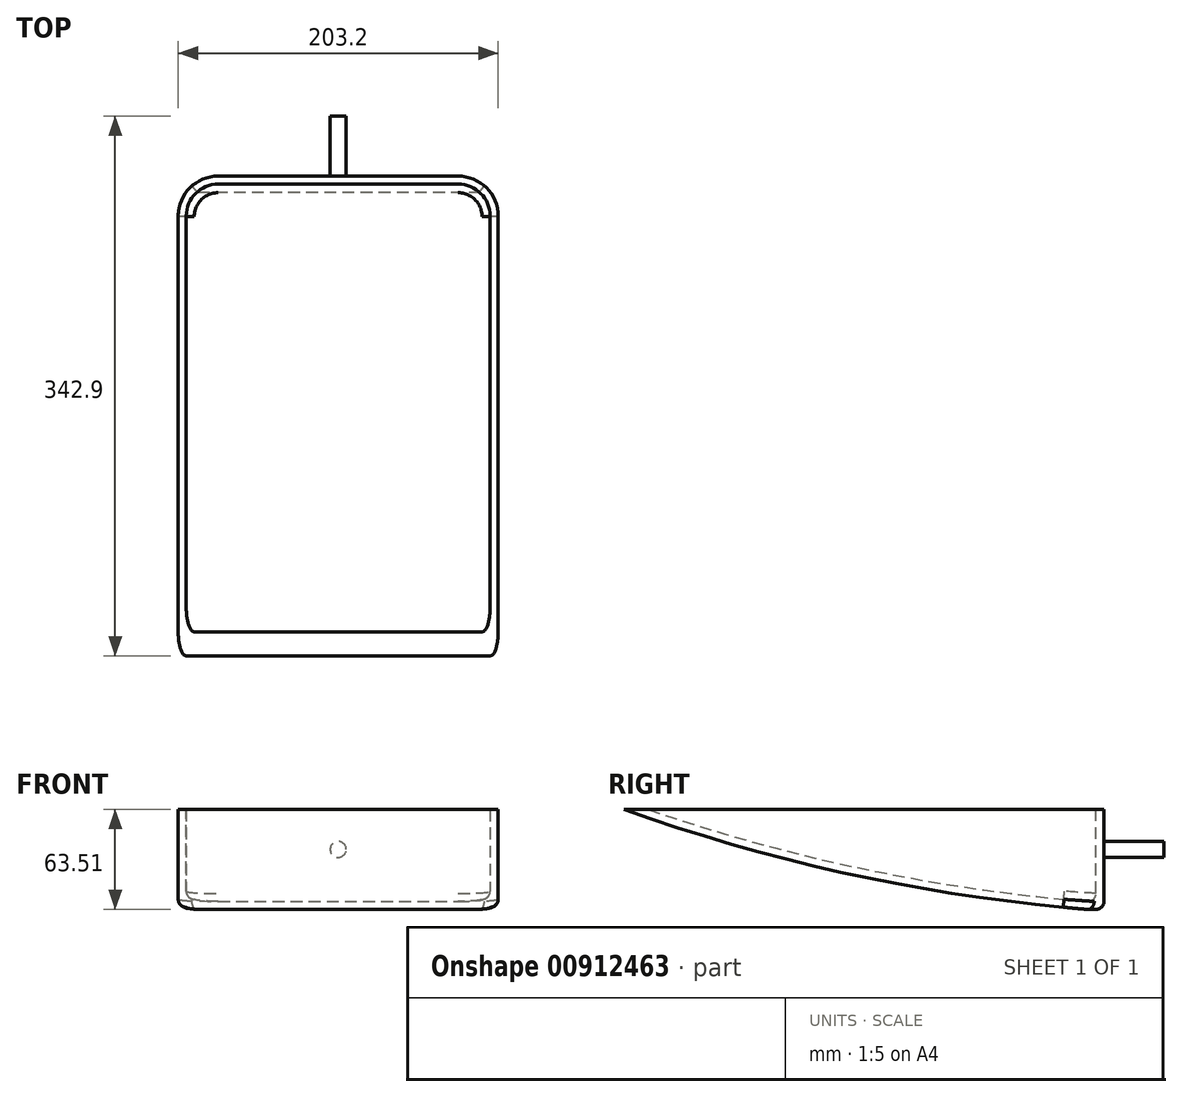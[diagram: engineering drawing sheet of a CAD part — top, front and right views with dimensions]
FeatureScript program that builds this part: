
annotation { "Feature Type Name" : "Feature", "Feature Type Description" : "" }
export const myFeature = defineFeature(function(context is Context, id is Id, definition is map)
    precondition{}
    {
        {
            var Q0;
            Q0=qCreatedBy(makeId("Top.planeOp"),FACE);
            var sketch = newSketch(context, id + "F0", { "sketchPlane" : qUnion([Q0])});
            skLineSegment(sketch, "E0.bottom", {"start": v(-50.23, 269.87) * mm, "end": v(152.97, 269.87) * mm});
            skLineSegment(sketch, "E0.top", {"start": v(-50.23, -34.93) * mm, "end": v(152.97, -34.93) * mm});
            skLineSegment(sketch, "E0.left", {"start": v(-50.23, 269.87) * mm, "end": v(-50.23, -34.93) * mm});
            skLineSegment(sketch, "E0.right", {"start": v(152.97, 269.87) * mm, "end": v(152.97, -34.93) * mm});
            skSolve(sketch);
        }
        {
            var Q0;
            Q0=makeQuery(id+"F0.imprint","IMPRINT",FACE,{"disambiguationData":[TD([[makeQuery(id+"F0.imprint","IMPRINT",EDGE,{"derivedFrom":sQuery(id+"F0.wireOp",EDGE,"E0.bottom")}),-1.0]])]});
            extrude(context, id + "F1", {"entities" : qUnion([Q0]), "depth" : 63.5 * mm, "offsetDistance" : 25.4 * mm});
        }
        {
            var Q0;
            Q0=makeQuery(id+"F1.opExtrude","SWEPT_FACE",FACE,{"disambiguationData":[OSD([sQuery(id+"F0.wireOp",EDGE,"E0.bottom")])]});
            var sketch = newSketch(context, id + "F2", { "sketchPlane" : qUnion([Q0])});
            skCircle(sketch, "E1", {"center": v(-51.37, 38.1) * mm, "radius": 5.08 * mm});
            skSolve(sketch);
        }
        {
            var Q0;
            Q0=makeQuery(id+"F2.imprint","IMPRINT",FACE,{"disambiguationData":[TD([[makeQuery(id+"F2.imprint","IMPRINT",EDGE,{"derivedFrom":sQuery(id+"F2.wireOp",EDGE,"E1")}),1.0]])]});
            extrude(context, id + "F3", {"entities" : qUnion([Q0]), "operationType" : NewBodyOperationType.ADD, "depth" : 38.1 * mm, "offsetDistance" : 25.4 * mm});
        }
        {
            var Q0;
            Q0=makeQuery(id+"F1.opExtrude","SWEPT_EDGE",EDGE,{"disambiguationData":[OSD([sQuery(id+"F0.wireOp",EDGE,"E0.bottom"),sQuery(id+"F0.wireOp",EDGE,"E0.left")])]});
            var Q1;
            Q1=makeQuery(id+"F1.opExtrude","SWEPT_EDGE",EDGE,{"disambiguationData":[OSD([sQuery(id+"F0.wireOp",EDGE,"E0.bottom"),sQuery(id+"F0.wireOp",EDGE,"E0.right")])]});
            fillet(context, id + "F4", {"entities" : qUnion([Q0, Q1]), "radius" : 25.4 * mm, "tangentPropagation" : true, "allowEdgeOverflow" : false});
        }
        {
            var Q0;
            Q0=makeQuery(id+"F1.opExtrude","SWEPT_FACE",FACE,{"disambiguationData":[OSD([sQuery(id+"F0.wireOp",EDGE,"E0.right")])]});
            var sketch = newSketch(context, id + "F5", { "sketchPlane" : qUnion([Q0])});
            skArc(sketch, "E2", {"start": v(-34.93, 63.5) * mm, "mid": v(110.25, 21.99) * mm, "end": v(259.63, 0) * mm});
            skLineSegment(sketch, "E3", {"start": v(-34.93, 63.5) * mm, "end": v(-61, -69.5) * mm});
            skLineSegment(sketch, "E4", {"start": v(-61, -69.5) * mm, "end": v(259.63, 0) * mm});
            skSolve(sketch);
        }
        {
            var Q0;
            {var subQ1=sQuery(id+"F0.wireOp",EDGE,"E0.right");var subQ6=makeQuery(id+"F1.opExtrude","CAP_EDGE",EDGE,{"disambiguationData":[OSD([subQ1])],"isStart":true});Q0=makeQuery(id+"F5.imprint","IMPRINT",FACE,{"disambiguationData":[TD([[makeQuery(id+"F5.imprint","IMPRINT",EDGE,{"derivedFrom":subQ6}),-1.0]])]});}
            var Q1;
            {var subQ3=sQuery(id+"F5.wireOp",EDGE,"E3");Q1=makeQuery(id+"F5.imprint","IMPRINT",FACE,{"disambiguationData":[TD([[makeQuery(id+"F5.imprint","IMPRINT",EDGE,{"derivedFrom":subQ3}),1.0]])]});}
            extrude(context, id + "F6", {"entities" : qUnion([Q0, Q1]), "operationType" : NewBodyOperationType.REMOVE, "endBound" : BoundingType.THROUGH_ALL, "oppositeDirection" : true, "depth" : 25.4 * mm, "offsetDistance" : 25.4 * mm});
        }
        {
            var Q0;
            Q0=makeQuery(id+"F1.opExtrude","CAP_FACE",FACE,{"disambiguationData":[OSD([sQuery(id+"F0.wireOp",EDGE,"E0.bottom"),sQuery(id+"F0.wireOp",EDGE,"E0.top"),sQuery(id+"F0.wireOp",EDGE,"E0.left"),sQuery(id+"F0.wireOp",EDGE,"E0.right")])],"isStart":false});
            shell(context, id + "F7", {"entities" : qUnion([Q0]), "thickness" : 5.08 * mm});
        }
        {
            var Q0;
            Q0=makeQuery(id+"F6.boolean.opBoolean","INTERSECT",EDGE,{"derivedFrom":[makeQuery(id+"F4.opFillet","BLEND_FACE",FACE,{"disambiguationData":[OSD([sQuery(id+"F0.wireOp",EDGE,"E0.bottom"),sQuery(id+"F0.wireOp",EDGE,"E0.right")])]}),makeQuery(id+"F6.opExtrude","SWEPT_FACE",FACE,{"disambiguationData":[OSD([sQuery(id+"F5.wireOp",EDGE,"E2")])]})]});
            var Q1;
            {var subQ0=sQuery(id+"F0.wireOp",EDGE,"E0.right");var subQ1=sQuery(id+"F0.wireOp",EDGE,"E0.bottom");Q1=makeQuery(id+"F4.opFillet","BLEND_EDGE",EDGE,{"blendedFrom":[makeQuery(id+"F1.opExtrude","SWEPT_EDGE",EDGE,{"disambiguationData":[OSD([subQ1,subQ0])]}),makeQuery(id+"F1.opExtrude","CAP_FACE",FACE,{"disambiguationData":[OSD([subQ1,sQuery(id+"F0.wireOp",EDGE,"E0.top"),sQuery(id+"F0.wireOp",EDGE,"E0.left"),subQ0])],"isStart":true})],"blendedInto":[makeQuery(id+"F1.opExtrude","CAP_FACE",FACE,{"disambiguationData":[OSD([subQ1,sQuery(id+"F0.wireOp",EDGE,"E0.top"),sQuery(id+"F0.wireOp",EDGE,"E0.left"),subQ0])],"isStart":true})]});}
            var Q2;
            Q2=makeQuery(id+"F6.boolean.opBoolean","INTERSECT",EDGE,{"derivedFrom":[makeQuery(id+"F1.opExtrude","SWEPT_FACE",FACE,{"disambiguationData":[OSD([sQuery(id+"F0.wireOp",EDGE,"E0.left")])]}),makeQuery(id+"F6.opExtrude","SWEPT_FACE",FACE,{"disambiguationData":[OSD([sQuery(id+"F5.wireOp",EDGE,"E2")])]})]});
            fillet(context, id + "F8", {"entities" : qUnion([Q0, Q1, Q2]), "radius" : 5.08 * mm, "tangentPropagation" : true, "allowEdgeOverflow" : false});
        }
        {
            var Q0;
            Q0=makeQuery(id+"F7.opShell","OFFSET_EDGE",EDGE,{"disambiguationData":[OSD([sQuery(id+"F0.wireOp",EDGE,"E0.left"),sQuery(id+"F5.wireOp",EDGE,"E2")])]});
            var Q1;
            Q1=makeQuery(id+"F7.opShell","OFFSET_EDGE",EDGE,{"disambiguationData":[OSD([sQuery(id+"F0.wireOp",EDGE,"E0.bottom"),sQuery(id+"F0.wireOp",EDGE,"E0.left"),sQuery(id+"F5.wireOp",EDGE,"E2")])]});
            var Q2;
            Q2=makeQuery(id+"F7.opShell","OFFSET_EDGE",EDGE,{"disambiguationData":[OSD([sQuery(id+"F5.wireOp",EDGE,"E2")])]});
            var Q3;
            {var subQ0=sQuery(id+"F0.wireOp",EDGE,"E0.right");var subQ1=sQuery(id+"F0.wireOp",EDGE,"E0.left");var subQ2=sQuery(id+"F0.wireOp",EDGE,"E0.top");var subQ3=sQuery(id+"F0.wireOp",EDGE,"E0.bottom");Q3=makeQuery(id+"F7.opShell","OFFSET_EDGE",EDGE,{"disambiguationData":[OSD([subQ3,subQ2,subQ1,subQ0]),TDD([makeQuery(id+"F4.opFillet","BLEND_EDGE",EDGE,{"blendedFrom":[makeQuery(id+"F1.opExtrude","SWEPT_EDGE",EDGE,{"disambiguationData":[OSD([subQ3,subQ0])]}),makeQuery(id+"F1.opExtrude","CAP_FACE",FACE,{"disambiguationData":[OSD([subQ3,subQ2,subQ1,subQ0])],"isStart":true})],"blendedInto":[makeQuery(id+"F1.opExtrude","CAP_FACE",FACE,{"disambiguationData":[OSD([subQ3,subQ2,subQ1,subQ0])],"isStart":true})]})])]});}
            var Q4;
            {var subQ0=sQuery(id+"F0.wireOp",EDGE,"E0.bottom");Q4=makeQuery(id+"F7.opShell","OFFSET_EDGE",EDGE,{"disambiguationData":[OSD([subQ0]),TDD([makeQuery(id+"F1.opExtrude","CAP_EDGE",EDGE,{"disambiguationData":[OSD([subQ0])],"isStart":true})])]});}
            var Q5;
            {var subQ0=sQuery(id+"F0.wireOp",EDGE,"E0.right");var subQ1=sQuery(id+"F0.wireOp",EDGE,"E0.left");var subQ2=sQuery(id+"F0.wireOp",EDGE,"E0.top");var subQ3=sQuery(id+"F0.wireOp",EDGE,"E0.bottom");Q5=makeQuery(id+"F7.opShell","OFFSET_EDGE",EDGE,{"disambiguationData":[OSD([subQ3,subQ2,subQ1,subQ0]),TDD([makeQuery(id+"F4.opFillet","BLEND_EDGE",EDGE,{"blendedFrom":[makeQuery(id+"F1.opExtrude","SWEPT_EDGE",EDGE,{"disambiguationData":[OSD([subQ3,subQ1])]}),makeQuery(id+"F1.opExtrude","CAP_FACE",FACE,{"disambiguationData":[OSD([subQ3,subQ2,subQ1,subQ0])],"isStart":true})],"blendedInto":[makeQuery(id+"F1.opExtrude","CAP_FACE",FACE,{"disambiguationData":[OSD([subQ3,subQ2,subQ1,subQ0])],"isStart":true})]})])]});}
            fillet(context, id + "F9", {"entities" : qUnion([Q0, Q1, Q2, Q3, Q4, Q5]), "radius" : 5.08 * mm, "tangentPropagation" : true, "allowEdgeOverflow" : false});
        }
    });
